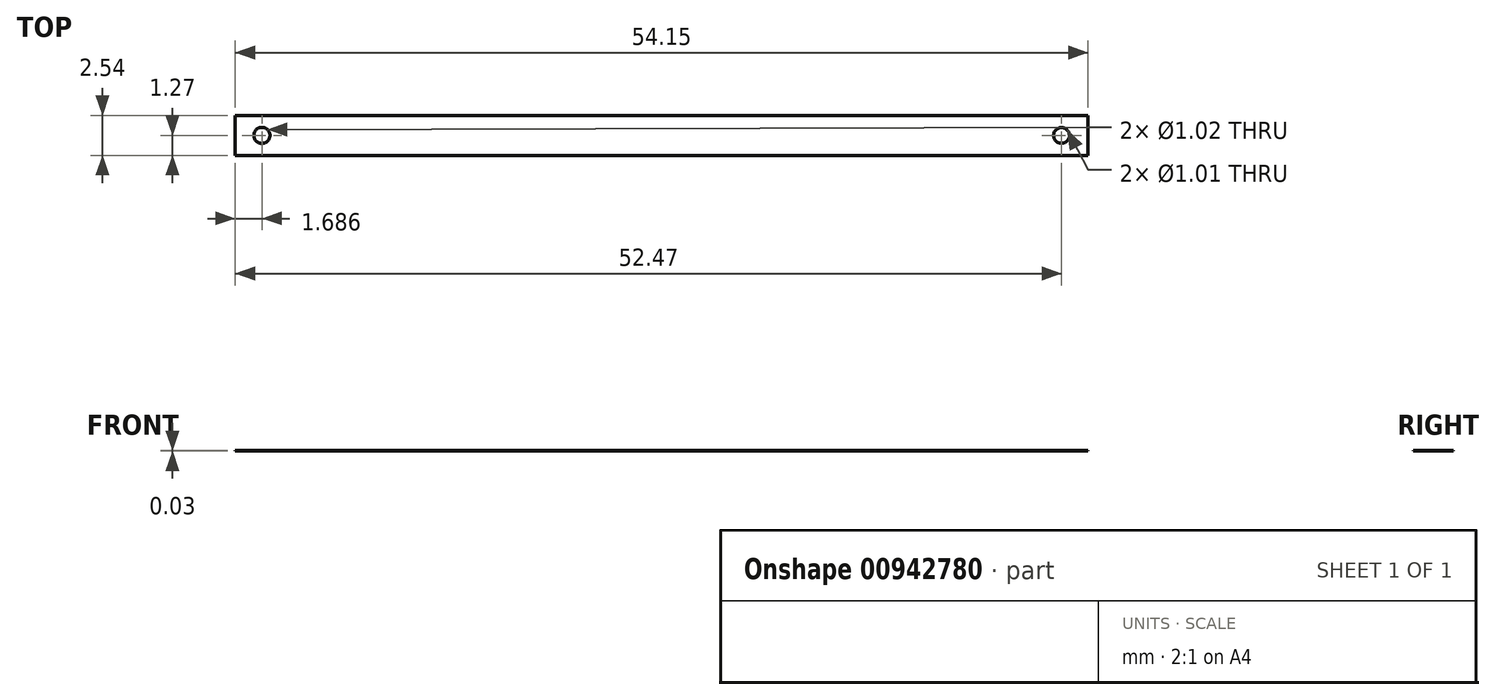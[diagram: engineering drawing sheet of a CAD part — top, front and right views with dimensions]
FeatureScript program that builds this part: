
annotation { "Feature Type Name" : "Feature", "Feature Type Description" : "" }
export const myFeature = defineFeature(function(context is Context, id is Id, definition is map)
    precondition{}
    {
        {
            var Q0;
            Q0=qCreatedBy(makeId("Top.planeOp"),FACE);
            var sketch = newSketch(context, id + "F0", { "sketchPlane" : qUnion([Q0])});
            skLineSegment(sketch, "E0.bottom", {"start": v(0, 0) * mm, "end": v(54.15, 0) * mm});
            skLineSegment(sketch, "E0.top", {"start": v(0, 2.54) * mm, "end": v(54.15, 2.54) * mm});
            skLineSegment(sketch, "E0.left", {"start": v(0, 0) * mm, "end": v(0, 2.54) * mm});
            skLineSegment(sketch, "E0.right", {"start": v(54.15, 0) * mm, "end": v(54.15, 2.54) * mm});
            skLineSegment(sketch, "E1", {"start": v(0, 1.27) * mm, "end": v(1.69, 1.27) * mm});
            skCircle(sketch, "E2", {"center": v(1.69, 1.27) * mm, "radius": 0.5 * mm});
            skLineSegment(sketch, "E3", {"start": v(54.15, 1.27) * mm, "end": v(52.47, 1.27) * mm});
            skCircle(sketch, "E4", {"center": v(52.47, 1.27) * mm, "radius": 0.5 * mm});
            skSolve(sketch);
        }
        {
            var Q0;
            {var subQ3=sQuery(id+"F0.wireOp",EDGE,"E0.bottom");Q0=makeQuery(id+"F0.imprint","IMPRINT",FACE,{"disambiguationData":[TD([[makeQuery(id+"F0.imprint","IMPRINT",EDGE,{"derivedFrom":subQ3}),1.0]])]});}
            extrude(context, id + "F1", {"entities" : qUnion([Q0]), "depth" : 0.03 * mm, "offsetDistance" : 25.4 * mm});
        }
    });
